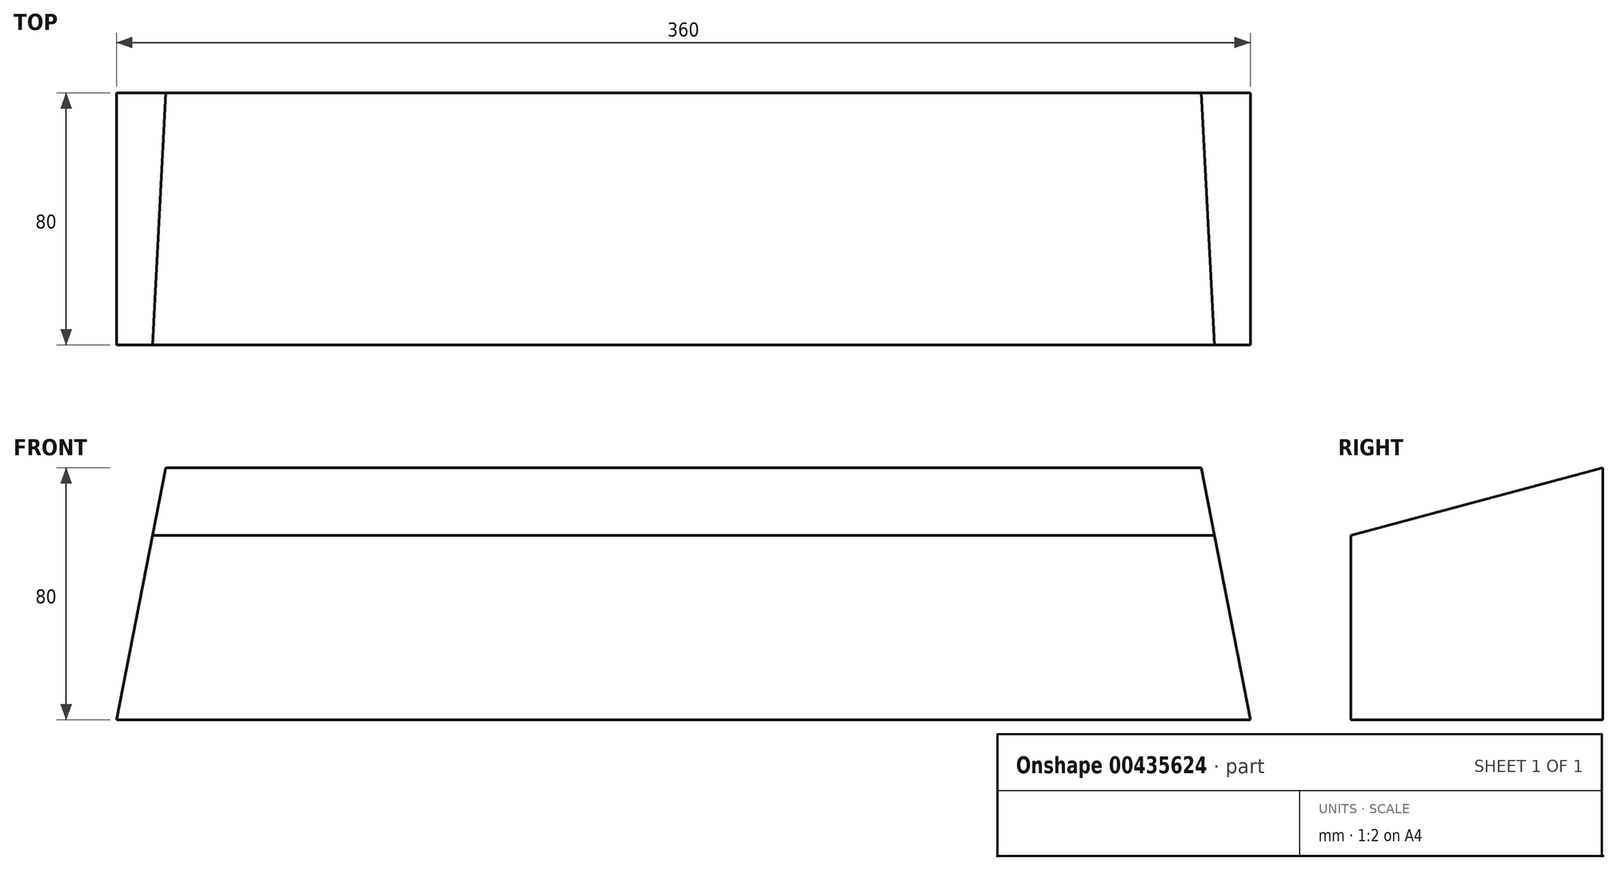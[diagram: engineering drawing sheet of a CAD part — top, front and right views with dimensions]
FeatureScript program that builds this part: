
annotation { "Feature Type Name" : "Feature", "Feature Type Description" : "" }
export const myFeature = defineFeature(function(context is Context, id is Id, definition is map)
    precondition{}
    {
        {
            var Q0;
            Q0=qCreatedBy(makeId("Front.planeOp"),FACE);
            var sketch = newSketch(context, id + "F0", { "sketchPlane" : qUnion([Q0])});
            skLineSegment(sketch, "E0", {"start": v(0, 0) * mm, "end": v(-180, 0) * mm});
            skLineSegment(sketch, "E1", {"start": v(-180, 0) * mm, "end": v(-164.42, 80) * mm});
            skLineSegment(sketch, "E2", {"start": v(-164.45, 0) * mm, "end": v(-269.4, 0) * mm, "construction": true});
            skLineSegment(sketch, "E3", {"start": v(-164.42, 80) * mm, "end": v(0, 80) * mm});
            skLineSegment(sketch, "E4", {"start": v(0, 0) * mm, "end": v(0, 159.9) * mm, "construction": true});
            skLineSegment(sketch, "E5.MirrorCS", {"start": v(164.42, 80) * mm, "end": v(0, 80) * mm});
            skLineSegment(sketch, "E6.MirrorCS", {"start": v(180, 0) * mm, "end": v(164.42, 80) * mm});
            skLineSegment(sketch, "E7.MirrorCS", {"start": v(0, 0) * mm, "end": v(180, 0) * mm});
            skSolve(sketch);
        }
        {
            var Q0;
            Q0 = qSketchRegion(id + "F0", true);
            extrude(context, id + "F1", {"entities" : qUnion([Q0]), "oppositeDirection" : true, "depth" : 80 * mm});
        }
        {
            var Q0;
            Q0=qCreatedBy(makeId("Right.planeOp"),FACE);
            var sketch = newSketch(context, id + "F2", { "sketchPlane" : qUnion([Q0])});
            skLineSegment(sketch, "E8", {"start": v(0, 0) * mm, "end": v(0, 80) * mm, "construction": true});
            skLineSegment(sketch, "E9", {"start": v(0, 80) * mm, "end": v(80, 80) * mm, "construction": true});
            skLineSegment(sketch, "E10", {"start": v(0, 59.63) * mm, "end": v(0, 80) * mm});
            skLineSegment(sketch, "E11", {"start": v(80, 80) * mm, "end": v(-39.13, 48.08) * mm});
            skLineSegment(sketch, "E12", {"start": v(-39.13, 48.08) * mm, "end": v(-39.13, 80) * mm});
            skLineSegment(sketch, "E13", {"start": v(-39.13, 80) * mm, "end": v(80, 80) * mm});
            skSolve(sketch);
        }
        {
            var Q0;
            Q0 = qSketchRegion(id + "F2", true);
            extrude(context, id + "F3", {"entities" : qUnion([Q0]), "operationType" : NewBodyOperationType.REMOVE, "oppositeDirection" : true, "depth" : 200 * mm, "hasSecondDirection" : true, "secondDirectionOppositeDirection" : false, "secondDirectionDepth" : 200 * mm});
        }
    });
